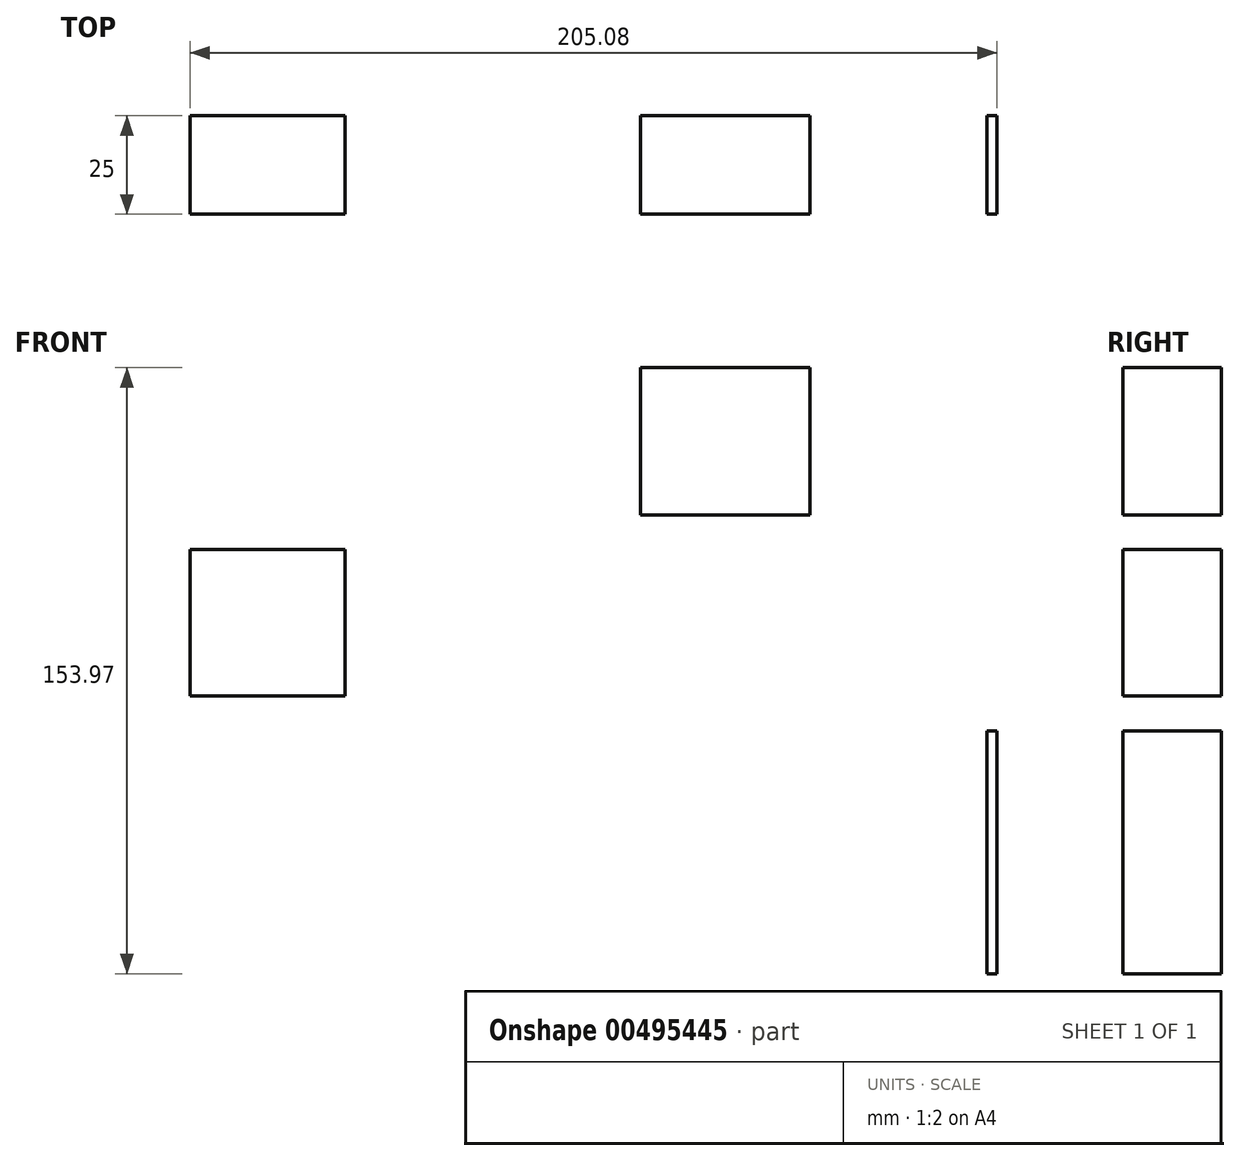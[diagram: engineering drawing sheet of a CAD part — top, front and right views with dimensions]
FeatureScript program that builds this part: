
annotation { "Feature Type Name" : "Feature", "Feature Type Description" : "" }
export const myFeature = defineFeature(function(context is Context, id is Id, definition is map)
    precondition{}
    {
        {
            var Q0;
            Q0=qCreatedBy(makeId("Front.planeOp"),FACE);
            var sketch = newSketch(context, id + "F0", { "sketchPlane" : qUnion([Q0])});
            skLineSegment(sketch, "E0.bottom", {"start": v(-75.62, 22.67) * mm, "end": v(-36.25, 22.67) * mm});
            skLineSegment(sketch, "E0.top", {"start": v(-75.62, -14.53) * mm, "end": v(-36.25, -14.53) * mm});
            skLineSegment(sketch, "E0.left", {"start": v(-75.62, 22.67) * mm, "end": v(-75.62, -14.53) * mm});
            skLineSegment(sketch, "E0.right", {"start": v(-36.25, 22.67) * mm, "end": v(-36.25, -14.53) * mm});
            skSolve(sketch);
        }
        {
            var Q0;
            Q0=makeQuery(id+"F0.imprint","IMPRINT",FACE,{"disambiguationData":[TD([[makeQuery(id+"F0.imprint","IMPRINT",EDGE,{"derivedFrom":sQuery(id+"F0.wireOp",EDGE,"E0.bottom")}),-1.0]])]});
            extrude(context, id + "F1", {"entities" : qUnion([Q0]), "depth" : 25 * mm});
        }
        {
            var Q0;
            Q0=qCreatedBy(makeId("Front.planeOp"),FACE);
            var sketch = newSketch(context, id + "F2", { "sketchPlane" : qUnion([Q0])});
            skLineSegment(sketch, "E1.bottom", {"start": v(129.46, -23.46) * mm, "end": v(126.87, -23.46) * mm});
            skLineSegment(sketch, "E1.top", {"start": v(129.46, -85.12) * mm, "end": v(126.87, -85.12) * mm});
            skLineSegment(sketch, "E1.left", {"start": v(129.46, -23.46) * mm, "end": v(129.46, -85.12) * mm});
            skLineSegment(sketch, "E1.right", {"start": v(126.87, -23.46) * mm, "end": v(126.87, -85.12) * mm});
            skLineSegment(sketch, "E2.bottom", {"start": v(81.91, 68.85) * mm, "end": v(38.89, 68.85) * mm});
            skLineSegment(sketch, "E2.top", {"start": v(81.91, 31.46) * mm, "end": v(38.89, 31.46) * mm});
            skLineSegment(sketch, "E2.left", {"start": v(81.91, 68.85) * mm, "end": v(81.91, 31.46) * mm});
            skLineSegment(sketch, "E2.right", {"start": v(38.89, 68.85) * mm, "end": v(38.89, 31.46) * mm});
            skSolve(sketch);
        }
        {
            var Q0;
            Q0=makeQuery(id+"F2.imprint","IMPRINT",FACE,{"disambiguationData":[TD([[makeQuery(id+"F2.imprint","IMPRINT",EDGE,{"derivedFrom":sQuery(id+"F2.wireOp",EDGE,"E1.bottom")}),1.0]])]});
            var Q1;
            Q1=makeQuery(id+"F2.imprint","IMPRINT",FACE,{"disambiguationData":[TD([[makeQuery(id+"F2.imprint","IMPRINT",EDGE,{"derivedFrom":sQuery(id+"F2.wireOp",EDGE,"E2.bottom")}),1.0]])]});
            extrude(context, id + "F3", {"entities" : qUnion([Q0, Q1]), "depth" : 25 * mm});
        }
    });
